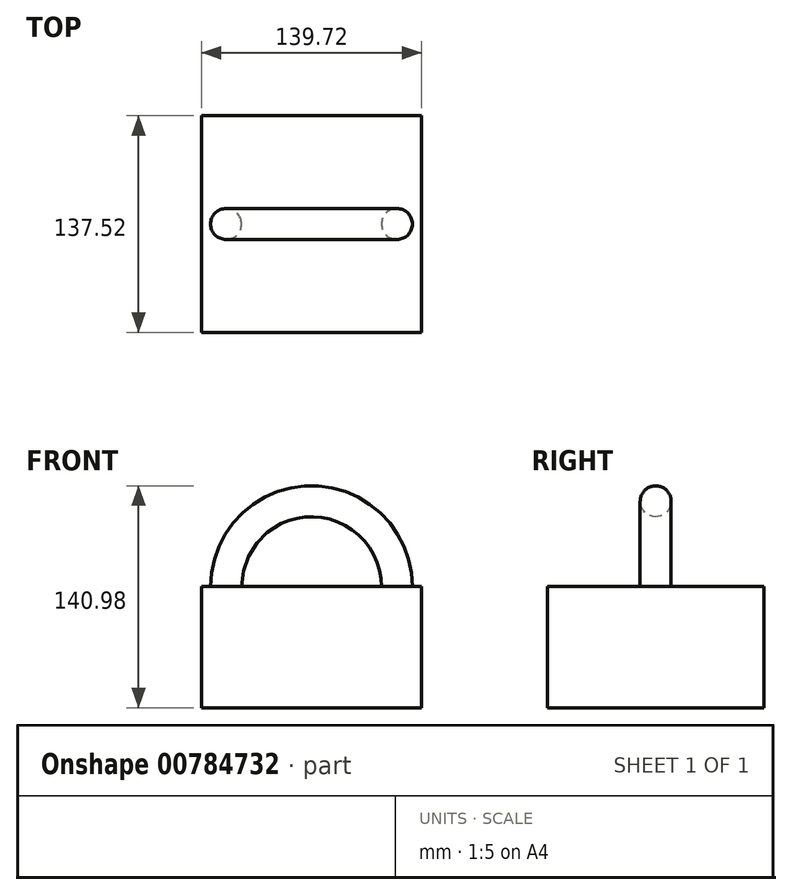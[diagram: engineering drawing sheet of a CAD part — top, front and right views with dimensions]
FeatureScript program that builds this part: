
annotation { "Feature Type Name" : "Feature", "Feature Type Description" : "" }
export const myFeature = defineFeature(function(context is Context, id is Id, definition is map)
    precondition{}
    {
        {
            var Q0;
            Q0=qCreatedBy(makeId("Top.planeOp"),FACE);
            var sketch = newSketch(context, id + "F0", { "sketchPlane" : qUnion([Q0])});
            skLineSegment(sketch, "E0.bottom", {"start": v(69.86, -68.76) * mm, "end": v(-69.86, -68.76) * mm});
            skLineSegment(sketch, "E0.top", {"start": v(69.86, 68.76) * mm, "end": v(-69.86, 68.76) * mm});
            skLineSegment(sketch, "E0.left", {"start": v(69.86, -68.76) * mm, "end": v(69.86, 68.76) * mm});
            skLineSegment(sketch, "E0.right", {"start": v(-69.86, -68.76) * mm, "end": v(-69.86, 68.76) * mm});
            skPoint(sketch, "E0.middle", {"position": v(0, 0) * mm});
            skLineSegment(sketch, "E1", {"start": v(0, 68.76) * mm, "end": v(0, -68.76) * mm});
            skSolve(sketch);
        }
        {
            var Q0;
            Q0=qCreatedBy(makeId("Top.planeOp"),FACE);
            var sketch = newSketch(context, id + "F1", { "sketchPlane" : qUnion([Q0])});
            skCircle(sketch, "E2", {"center": v(54.26, 0) * mm, "radius": 9.82 * mm});
            skSolve(sketch);
        }
        {
            var Q0;
            {var subQ0=sQuery(id+"F0.wireOp",EDGE,"E0.right");Q0=makeQuery(id+"F0.imprint","IMPRINT",FACE,{"disambiguationData":[TD([[makeQuery(id+"F0.imprint","IMPRINT",EDGE,{"derivedFrom":subQ0}),-1.0]])]});}
            var Q1;
            {var subQ0=sQuery(id+"F0.wireOp",EDGE,"E0.left");Q1=makeQuery(id+"F0.imprint","IMPRINT",FACE,{"disambiguationData":[TD([[makeQuery(id+"F0.imprint","IMPRINT",EDGE,{"derivedFrom":subQ0}),1.0]])]});}
            extrude(context, id + "F2", {"entities" : qUnion([Q0, Q1]), "oppositeDirection" : true, "depth" : 76.9 * mm, "offsetDistance" : 25.4 * mm});
        }
        {
            var Q0;
            Q0=makeQuery(id+"F1.imprint","IMPRINT",FACE,{"disambiguationData":[TD([[makeQuery(id+"F1.imprint","IMPRINT",EDGE,{"derivedFrom":sQuery(id+"F1.wireOp",EDGE,"E2")}),1.0]])]});
            var Q1;
            Q1=sQuery(id+"F0.wireOp",EDGE,"E1");
            revolve(context, id + "F3", {"operationType" : NewBodyOperationType.ADD, "entities" : qUnion([Q0]), "axis" : qUnion([Q1]), "revolveType" : RevolveType.FULL, "surfaceOperationType" : NewSurfaceOperationType.NEW});
        }
    });
